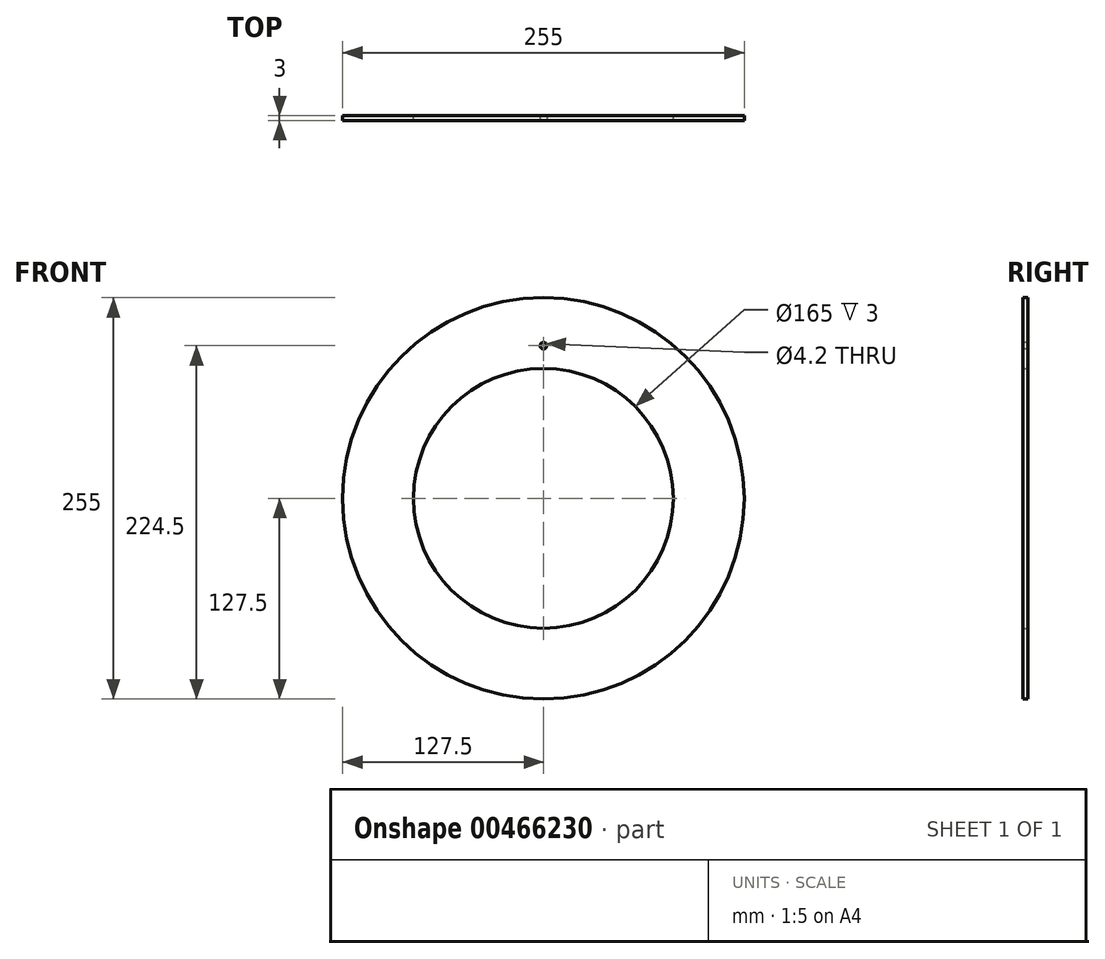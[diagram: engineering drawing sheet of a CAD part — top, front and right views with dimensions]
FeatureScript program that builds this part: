
annotation { "Feature Type Name" : "Feature", "Feature Type Description" : "" }
export const myFeature = defineFeature(function(context is Context, id is Id, definition is map)
    precondition{}
    {
        {
            var Q0;
            Q0=qCreatedBy(makeId("Front.planeOp"),FACE);
            var sketch = newSketch(context, id + "F0", { "sketchPlane" : qUnion([Q0])});
            skCircle(sketch, "E0", {"center": v(0, 0) * mm, "radius": 127.5 * mm});
            skCircle(sketch, "E1", {"center": v(0, 0) * mm, "radius": 82.5 * mm});
            skCircle(sketch, "E2", {"center": v(0, 0) * mm, "radius": 97 * mm, "construction": true});
            skSolve(sketch);
        }
        {
            var Q0;
            Q0 = qSketchRegion(id + "F0", true);
            extrude(context, id + "F1", {"entities" : qUnion([Q0]), "depth" : 3 * mm, "offsetDistance" : 25 * mm});
        }
        {
            var Q0;
            Q0=makeQuery(id+"F1.opExtrude","CAP_FACE",FACE,{"disambiguationData":[OSD([sQuery(id+"F0.wireOp",EDGE,"E0"),sQuery(id+"F0.wireOp",EDGE,"E1")])],"isStart":false});
            var sketch = newSketch(context, id + "F2", { "sketchPlane" : qUnion([Q0])});
            skCircle(sketch, "E3", {"center": v(0, 0) * mm, "radius": 97 * mm, "construction": true});
            skLineSegment(sketch, "E4", {"start": v(0, 0) * mm, "end": v(0, 97) * mm, "construction": true});
            skCircle(sketch, "E5", {"center": v(0, 97) * mm, "radius": 2.1 * mm});
            skSolve(sketch);
        }
        {
            var Q0;
            Q0 = qSketchRegion(id + "F2", true);
            extrude(context, id + "F3", {"entities" : qUnion([Q0]), "operationType" : NewBodyOperationType.REMOVE, "endBound" : BoundingType.UP_TO_NEXT, "oppositeDirection" : true, "depth" : 25 * mm, "offsetDistance" : 25 * mm});
        }
    });
